# Revit family: 4f
name_source: partatom
category: Pipe Accessories
revit_build: Autodesk Revit 2018 (Build: 20170223_1515(x64)
units: mm (PartAtom-declared; Revit-internal decimal feet)

## family parameters
Cut with Voids When Loaded = No
Host = Face
OmniClass Number = 23.27.43.00
OmniClass Title = Pipe Fittings
Part Type = Normal
Round Connector Dimension = Use Diameter
Shared = No

## types (2) — shared parameters
Assembly Code = D2040100
BIMobject category = Joints
Default Elevation = 1219 mm
Description = Flange Kit
Design country = Italy
Edition number = 1
IFC Classification = Pipe Fitting
Keynote = 15410
Lookup Table Name = Flange Kit - 90019
Manufacturer = Aignep Spa
Manufacturer country = Italy
Manufacturer name = Aignep Spa
Material main = Steel
Model = 90019
OmniClass Code = 23-27 43 00
OmniClass Description = Pipe Fittings
Product Guid = 93031174-efef-4b5c-b675-794ecca6ef6c
Product Material = AIGNEP - Steel - Brushed
Product SKU = Flange-Kit-90019
Product certification = https://www.aignep.com
Product data url = https://www.bimobject.com
Product family = INFINITY
Product group = Screw
Product name = Flange Kit - 90019
Product url = https://www.aignep.com
QR code = https://www.bimobject.com
URL = https://www.aignep.com
s1 = 3 mm  [stored 0.00984252 ft]

## per-type parameters (varying)
| type | A | Bolt Diameter | L | L1 | d | s2 | s3 |
| M16 | 24 mm  [stored 0.0787402 ft] | 16 mm  [stored 0.0524934 ft] | 70 mm  [stored 0.229659 ft] | 50 mm  [stored 0.164042 ft] | 27 mm  [stored 0.0885827 ft] | 10 mm  [stored 0.0328084 ft] | 16 mm  [stored 0.0524934 ft] |
| M20 | 35 mm  [stored 0.114829 ft] | 20 mm  [stored 0.0656168 ft] | 80 mm  [stored 0.262467 ft] | 54 mm  [stored 0.177165 ft] | 37 mm  [stored 0.121391 ft] | 13 mm | 19 mm  [stored 0.062336 ft] |

note: [stored X ft] marks values corroborated as IEEE doubles in the binary element streams (Revit-internal decimal feet)

## geometry (parser evidence)
native form markers: Sweep x3
no freeform markers — native parametric forms only
